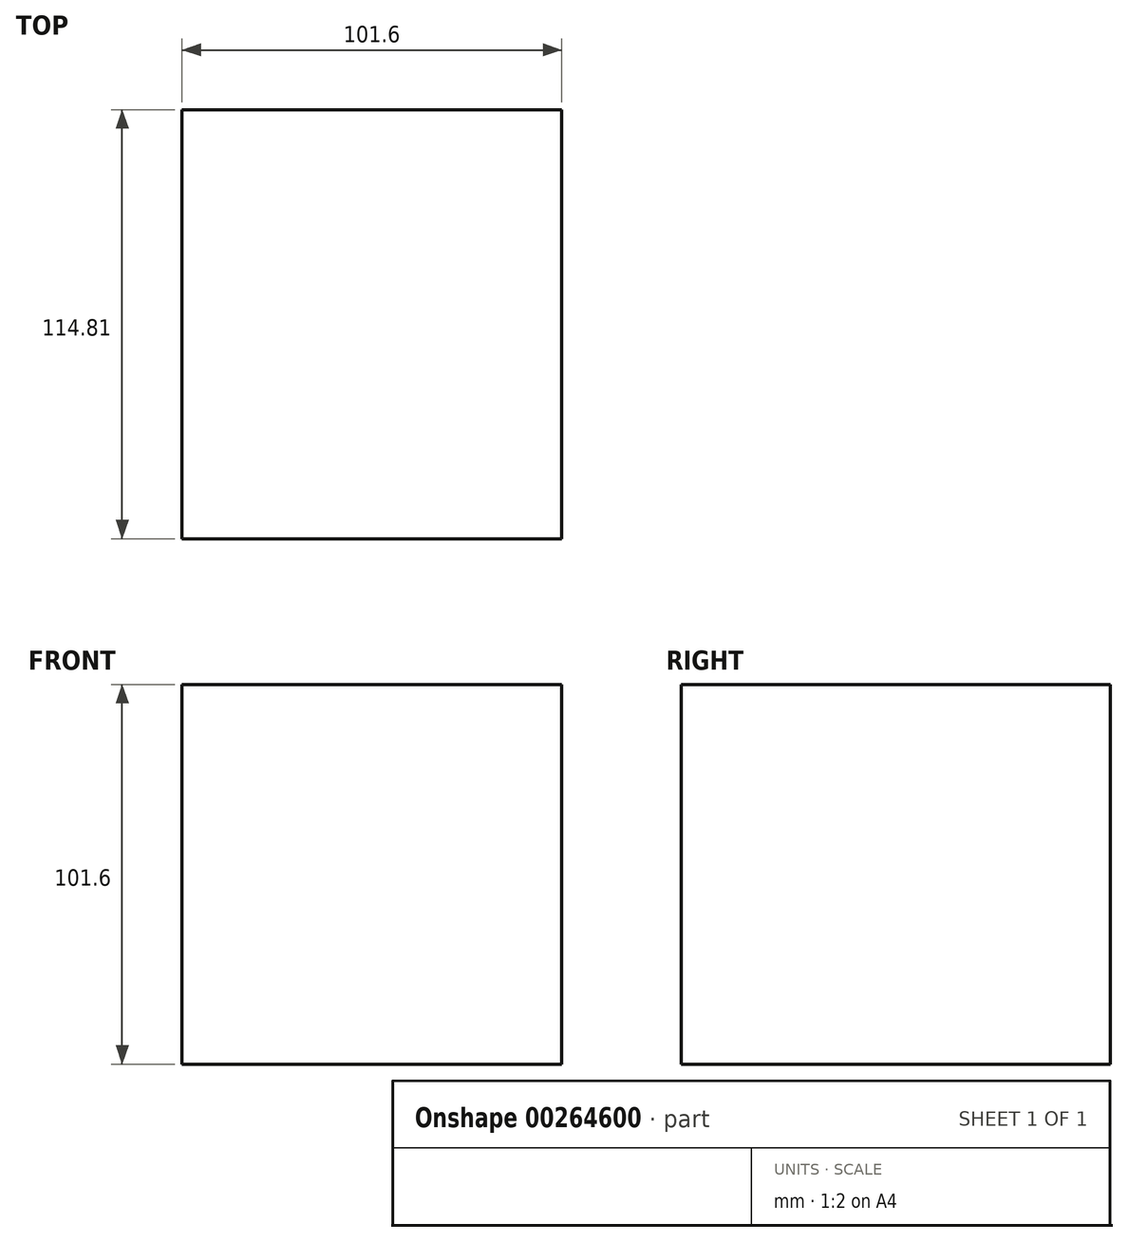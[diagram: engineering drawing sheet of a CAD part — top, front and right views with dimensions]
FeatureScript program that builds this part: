
annotation { "Feature Type Name" : "Feature", "Feature Type Description" : "" }
export const myFeature = defineFeature(function(context is Context, id is Id, definition is map)
    precondition{}
    {
        {
            var Q0;
            Q0=qCreatedBy(makeId("Front.planeOp"),FACE);
            var sketch = newSketch(context, id + "F0", { "sketchPlane" : qUnion([Q0])});
            skLineSegment(sketch, "E0.bottom", {"start": v(0, 0) * mm, "end": v(-101.6, 0) * mm});
            skLineSegment(sketch, "E0.top", {"start": v(0, 101.6) * mm, "end": v(-101.6, 101.6) * mm});
            skLineSegment(sketch, "E0.left", {"start": v(0, 0) * mm, "end": v(0, 101.6) * mm});
            skLineSegment(sketch, "E0.right", {"start": v(-101.6, 0) * mm, "end": v(-101.6, 101.6) * mm});
            skSolve(sketch);
        }
        {
            var Q0;
            Q0=makeQuery(id+"F0.imprint","IMPRINT",FACE,{"disambiguationData":[TD([[makeQuery(id+"F0.imprint","IMPRINT",EDGE,{"derivedFrom":sQuery(id+"F0.wireOp",EDGE,"E0.bottom")}),-1.0]])]});
            extrude(context, id + "F1", {"entities" : qUnion([Q0]), "depth" : 114.8 * mm});
        }
    });
